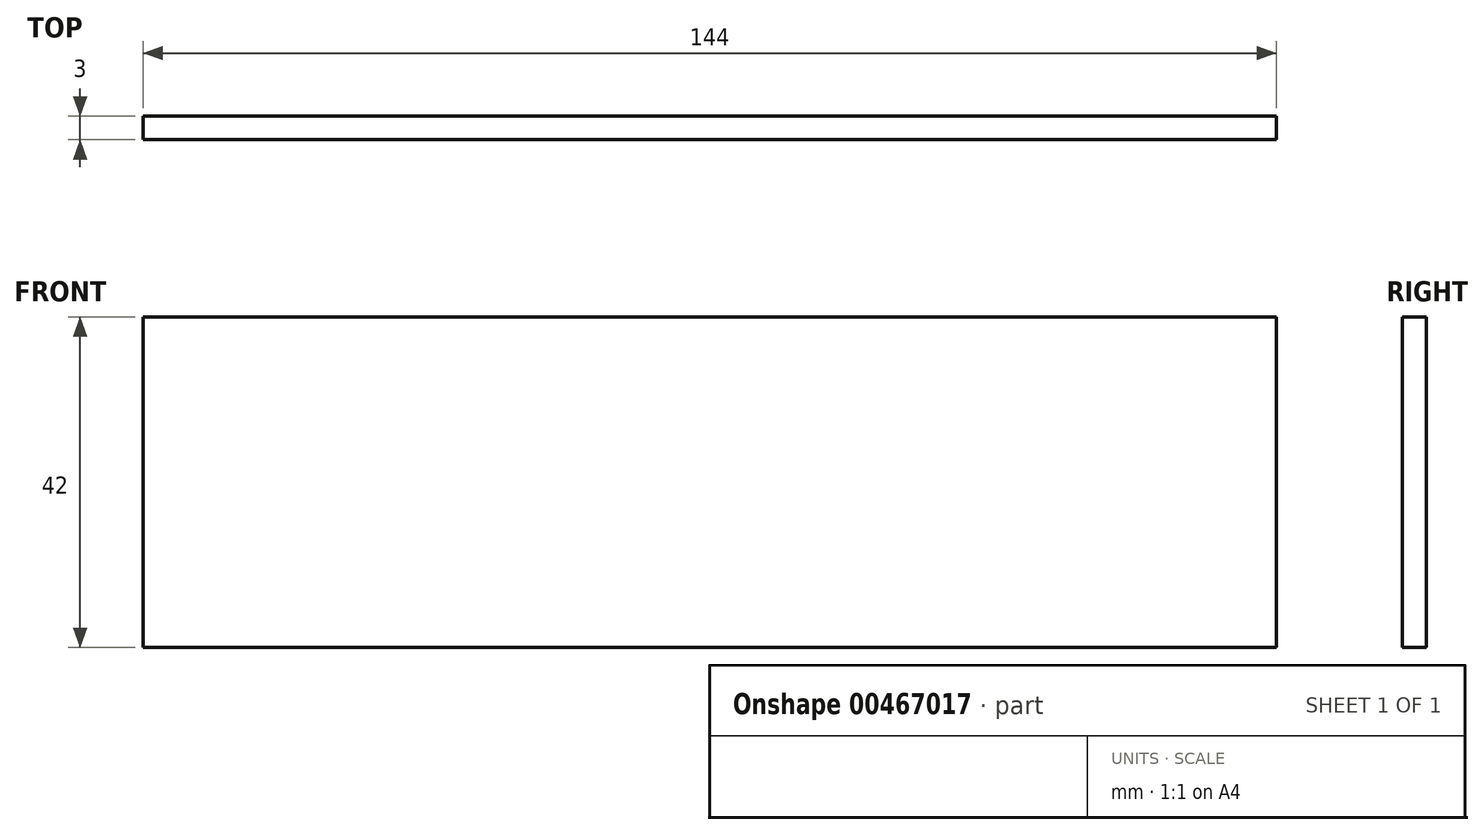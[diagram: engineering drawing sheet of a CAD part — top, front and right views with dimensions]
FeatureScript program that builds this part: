
annotation { "Feature Type Name" : "Feature", "Feature Type Description" : "" }
export const myFeature = defineFeature(function(context is Context, id is Id, definition is map)
    precondition{}
    {
        {
            var Q0;
            Q0=qCreatedBy(makeId("Front.planeOp"),FACE);
            var sketch = newSketch(context, id + "F0", { "sketchPlane" : qUnion([Q0])});
            skLineSegment(sketch, "E0.bottom", {"start": v(0, 0) * mm, "end": v(144, 0) * mm});
            skLineSegment(sketch, "E0.top", {"start": v(0, 42) * mm, "end": v(144, 42) * mm});
            skLineSegment(sketch, "E0.left", {"start": v(0, 0) * mm, "end": v(0, 42) * mm});
            skLineSegment(sketch, "E0.right", {"start": v(144, 0) * mm, "end": v(144, 42) * mm});
            skSolve(sketch);
        }
        {
            var Q0;
            Q0=makeQuery(id+"F0.imprint","IMPRINT",FACE,{"disambiguationData":[TD([[makeQuery(id+"F0.imprint","IMPRINT",EDGE,{"derivedFrom":sQuery(id+"F0.wireOp",EDGE,"E0.bottom")}),1.0]])]});
            extrude(context, id + "F1", {"entities" : qUnion([Q0]), "depth" : 3 * mm});
        }
    });
